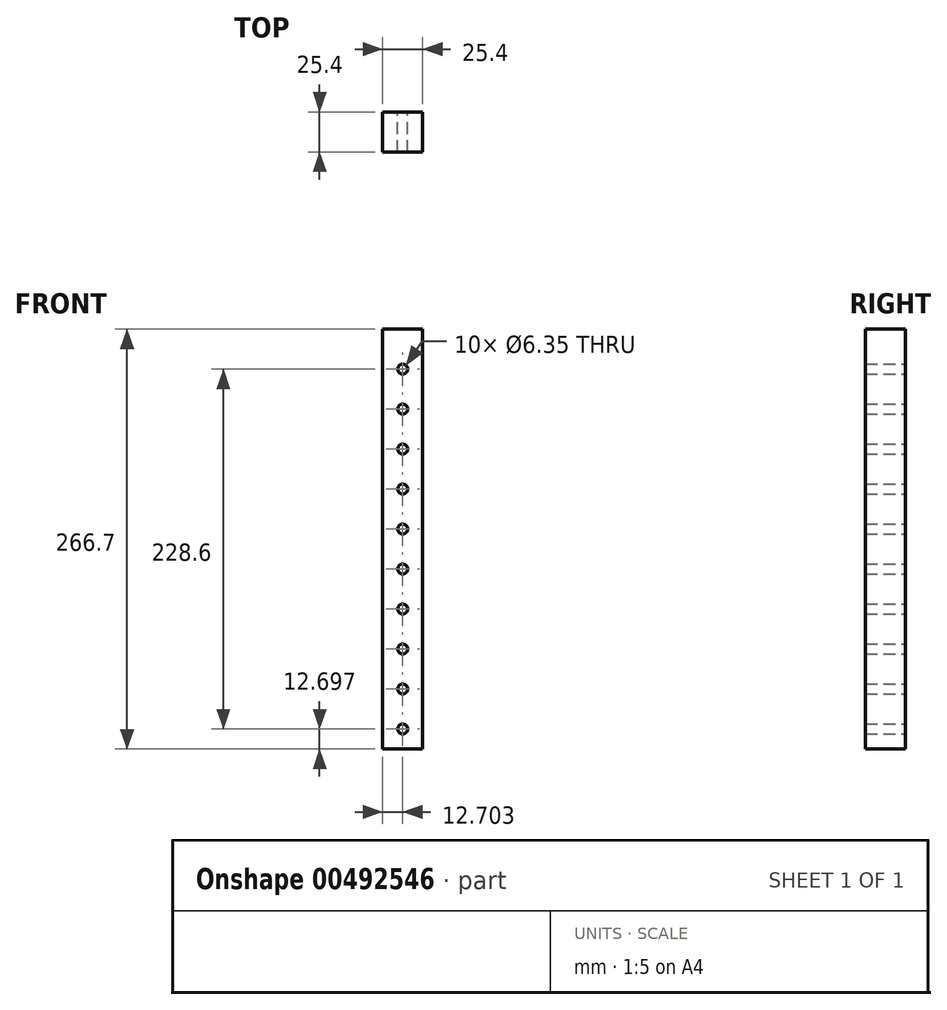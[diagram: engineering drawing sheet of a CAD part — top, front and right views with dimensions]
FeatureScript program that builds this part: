
annotation { "Feature Type Name" : "Feature", "Feature Type Description" : "" }
export const myFeature = defineFeature(function(context is Context, id is Id, definition is map)
    precondition{}
    {
        {
            var Q0;
            Q0=qCreatedBy(makeId("Front.planeOp"),FACE);
            var sketch = newSketch(context, id + "F0", { "sketchPlane" : qUnion([Q0])});
            skLineSegment(sketch, "E0.bottom", {"start": v(-24.66, 225.74) * mm, "end": v(0.74, 225.74) * mm});
            skLineSegment(sketch, "E0.top", {"start": v(-24.66, -40.96) * mm, "end": v(0.74, -40.96) * mm});
            skLineSegment(sketch, "E0.left", {"start": v(-24.66, 225.74) * mm, "end": v(-24.66, -40.96) * mm});
            skLineSegment(sketch, "E0.right", {"start": v(0.74, 225.74) * mm, "end": v(0.74, -40.96) * mm});
            skCircle(sketch, "E1", {"center": v(-11.96, -28.26) * mm, "radius": 3.18 * mm});
            skCircle(sketch, "E2.0.1.0", {"center": v(-11.96, -2.86) * mm, "radius": 3.18 * mm});
            skCircle(sketch, "E2.0.2.0", {"center": v(-11.96, 22.54) * mm, "radius": 3.18 * mm});
            skCircle(sketch, "E2.0.3.0", {"center": v(-11.96, 47.94) * mm, "radius": 3.18 * mm});
            skCircle(sketch, "E2.0.4.0", {"center": v(-11.96, 73.34) * mm, "radius": 3.18 * mm});
            skCircle(sketch, "E2.0.5.0", {"center": v(-11.96, 98.74) * mm, "radius": 3.18 * mm});
            skCircle(sketch, "E2.0.6.0", {"center": v(-11.96, 124.14) * mm, "radius": 3.18 * mm});
            skCircle(sketch, "E2.0.7.0", {"center": v(-11.96, 149.54) * mm, "radius": 3.18 * mm});
            skCircle(sketch, "E2.0.8.0", {"center": v(-11.96, 174.94) * mm, "radius": 3.18 * mm});
            skCircle(sketch, "E2.0.9.0", {"center": v(-11.96, 200.34) * mm, "radius": 3.18 * mm});
            skLineSegment(sketch, "E2.direction1", {"start": v(-11.96, -28.26) * mm, "end": v(13.44, -28.26) * mm, "construction": true});
            skLineSegment(sketch, "E2.direction2", {"start": v(-11.96, -28.26) * mm, "end": v(-11.96, -2.86) * mm, "construction": true});
            skSolve(sketch);
        }
        {
            var Q0;
            Q0=makeQuery(id+"F0.imprint","IMPRINT",FACE,{"disambiguationData":[TD([[makeQuery(id+"F0.imprint","IMPRINT",EDGE,{"derivedFrom":sQuery(id+"F0.wireOp",EDGE,"E0.bottom")}),-1.0]])]});
            extrude(context, id + "F1", {"entities" : qUnion([Q0]), "depth" : 25.4 * mm});
        }
    });
